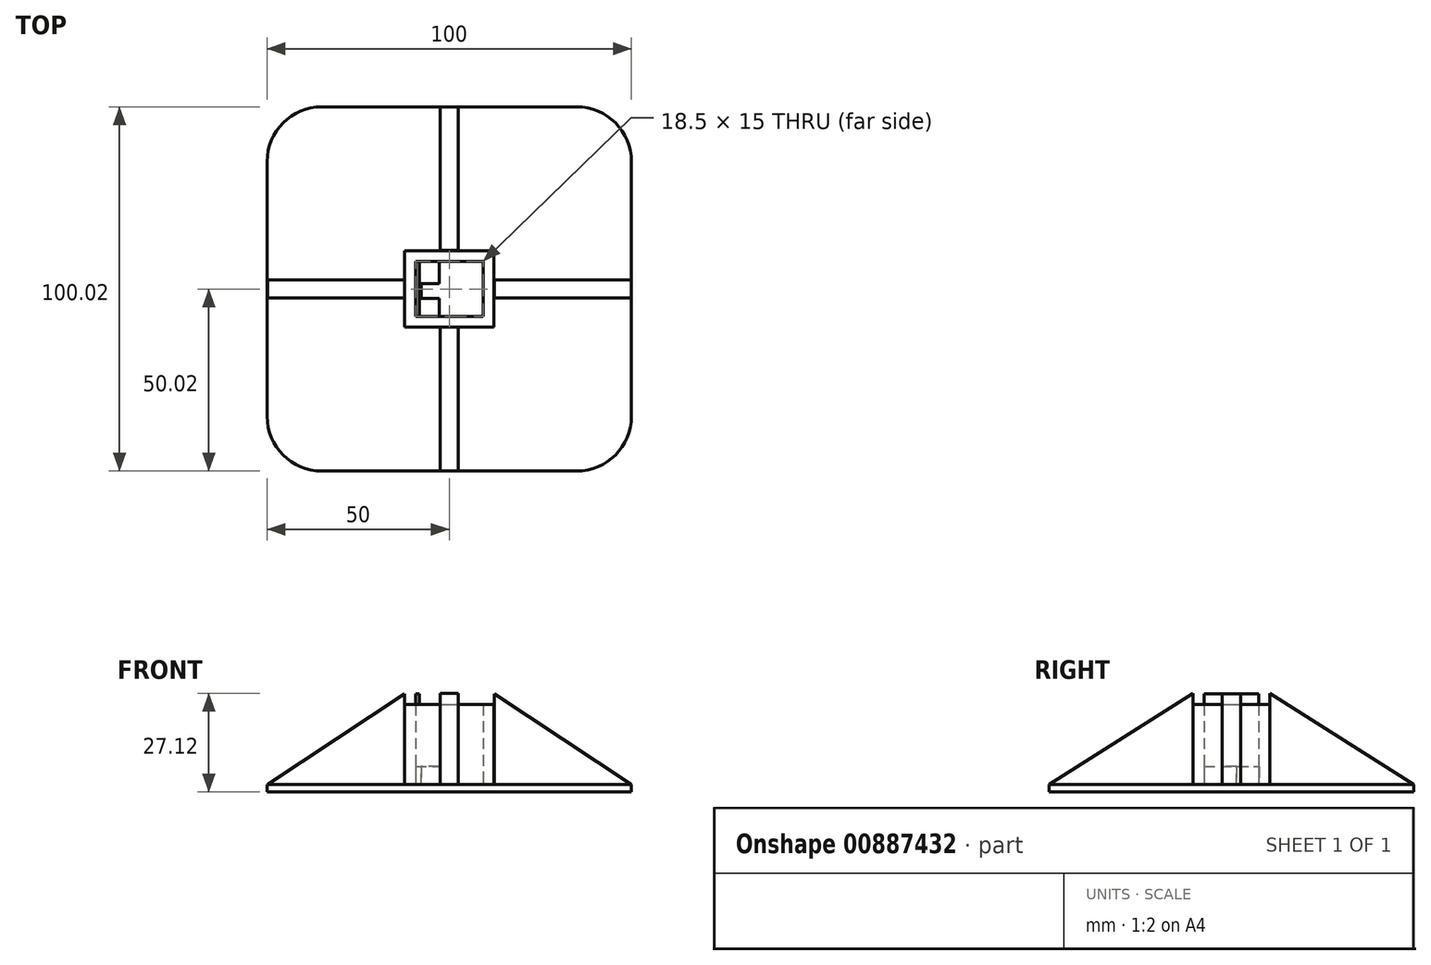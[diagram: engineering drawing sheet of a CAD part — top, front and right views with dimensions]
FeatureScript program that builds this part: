
annotation { "Feature Type Name" : "Feature", "Feature Type Description" : "" }
export const myFeature = defineFeature(function(context is Context, id is Id, definition is map)
    precondition{}
    {
        {
            var Q0;
            Q0=qCreatedBy(makeId("Top.planeOp"),FACE);
            var sketch = newSketch(context, id + "F0", { "sketchPlane" : qUnion([Q0])});
            skLineSegment(sketch, "E0.bottom", {"start": v(-50, -50) * mm, "end": v(50, -50) * mm});
            skLineSegment(sketch, "E0.top", {"start": v(-50, 50) * mm, "end": v(50, 50) * mm});
            skLineSegment(sketch, "E0.left", {"start": v(-50, -50) * mm, "end": v(-50, 50) * mm});
            skLineSegment(sketch, "E0.right", {"start": v(50, -50) * mm, "end": v(50, 50) * mm});
            skPoint(sketch, "E0.middle", {"position": v(0, 0) * mm});
            skSolve(sketch);
        }
        {
            var Q0;
            Q0=qCreatedBy(makeId("Top.planeOp"),FACE);
            var sketch = newSketch(context, id + "F1", { "sketchPlane" : qUnion([Q0])});
            skLineSegment(sketch, "E1.bottom", {"start": v(-9.25, -7.5) * mm, "end": v(9.25, -7.5) * mm});
            skLineSegment(sketch, "E1.top", {"start": v(-9.25, 7.5) * mm, "end": v(9.25, 7.5) * mm});
            skLineSegment(sketch, "E1.left", {"start": v(-9.25, -7.5) * mm, "end": v(-9.25, 7.5) * mm});
            skLineSegment(sketch, "E1.right", {"start": v(9.25, -7.5) * mm, "end": v(9.25, 7.5) * mm});
            skPoint(sketch, "E1.middle", {"position": v(0, 0) * mm});
            skLineSegment(sketch, "E2.0", {"start": v(-12.25, 10.5) * mm, "end": v(12.25, 10.5) * mm});
            skLineSegment(sketch, "E2.1", {"start": v(-12.25, -10.5) * mm, "end": v(-12.25, 10.5) * mm});
            skLineSegment(sketch, "E2.2", {"start": v(-12.25, -10.5) * mm, "end": v(12.25, -10.5) * mm});
            skLineSegment(sketch, "E2.3", {"start": v(12.25, -10.5) * mm, "end": v(12.25, 10.5) * mm});
            skSolve(sketch);
        }
        {
            var Q0;
            Q0 = qSketchRegion(id + "F1", true);
            extrude(context, id + "F2", {"entities" : qUnion([Q0]), "depth" : 22 * mm, "offsetDistance" : 25 * mm});
        }
        {
            var Q0;
            Q0=makeQuery(id+"F2.opExtrude","CAP_FACE",FACE,{"disambiguationData":[OSD([sQuery(id+"F1.wireOp",EDGE,"E1.bottom"),sQuery(id+"F1.wireOp",EDGE,"E1.top"),sQuery(id+"F1.wireOp",EDGE,"E1.left"),sQuery(id+"F1.wireOp",EDGE,"E1.right"),sQuery(id+"F1.wireOp",EDGE,"E2.0"),sQuery(id+"F1.wireOp",EDGE,"E2.1"),sQuery(id+"F1.wireOp",EDGE,"E2.2"),sQuery(id+"F1.wireOp",EDGE,"E2.3")])],"isStart":false});
            var sketch = newSketch(context, id + "F3", { "sketchPlane" : qUnion([Q0])});
            skLineSegment(sketch, "E3.bottom", {"start": v(-9.25, -7.5) * mm, "end": v(9.25, -7.5) * mm});
            skLineSegment(sketch, "E3.top", {"start": v(-9.25, 7.5) * mm, "end": v(9.25, 7.5) * mm});
            skLineSegment(sketch, "E3.left", {"start": v(-9.25, -7.5) * mm, "end": v(-9.25, 7.5) * mm});
            skLineSegment(sketch, "E3.right", {"start": v(9.25, -7.5) * mm, "end": v(9.25, 7.5) * mm});
            skPoint(sketch, "E3.middle", {"position": v(0, 0) * mm});
            skLineSegment(sketch, "E4.0", {"start": v(-8.25, -7.5) * mm, "end": v(-8.25, 7.5) * mm});
            skLineSegment(sketch, "E5.0", {"start": v(-12.25, 10.5) * mm, "end": v(12.25, 10.5) * mm});
            skLineSegment(sketch, "E5.1", {"start": v(-12.25, -10.5) * mm, "end": v(-12.25, 10.5) * mm});
            skLineSegment(sketch, "E5.2", {"start": v(-12.25, -10.5) * mm, "end": v(12.25, -10.5) * mm});
            skLineSegment(sketch, "E5.3", {"start": v(12.25, -10.5) * mm, "end": v(12.25, 10.5) * mm});
            skSolve(sketch);
        }
        {
            var Q0;
            {var subQ4=sQuery(id+"F3.wireOp",EDGE,"E3.left");Q0=makeQuery(id+"F3.imprint","IMPRINT",FACE,{"disambiguationData":[TD([[makeQuery(id+"F3.imprint","IMPRINT",EDGE,{"derivedFrom":subQ4}),1.0]])]});}
            var sketch = newSketch(context, id + "F4", { "sketchPlane" : qUnion([Q0])});
            skSolve(sketch);
        }
        {
            var Q0;
            {var subQ4=sQuery(id+"F3.wireOp",EDGE,"E3.left");Q0=makeQuery(id+"F4.imprint","IMPRINT",FACE,{"disambiguationData":[TD([[makeQuery(id+"F4.imprint","IMPRINT",EDGE,{"derivedFrom":makeQuery(id+"F3.imprint","IMPRINT",EDGE,{"derivedFrom":subQ4})}),1.0]])]});}
            var Q1;
            {var subQ0=sQuery(id+"F3.wireOp",EDGE,"E3.left");Q1=makeQuery(id+"F3.imprint","IMPRINT",FACE,{"disambiguationData":[TD([[makeQuery(id+"F3.imprint","IMPRINT",EDGE,{"derivedFrom":subQ0}),-1.0]])]});}
            extrude(context, id + "F5", {"entities" : qUnion([Q0, Q1]), "operationType" : NewBodyOperationType.ADD, "depth" : 3 * mm, "offsetDistance" : 25 * mm});
        }
        {
            var Q0;
            Q0=qCreatedBy(makeId("Top.planeOp"),FACE);
            var sketch = newSketch(context, id + "F6", { "sketchPlane" : qUnion([Q0])});
            skLineSegment(sketch, "E6", {"start": v(-2.74, 1.46) * mm, "end": v(-7.74, 1.46) * mm});
            skLineSegment(sketch, "E7", {"start": v(-7.74, -2.54) * mm, "end": v(-2.74, -2.54) * mm});
            skLineSegment(sketch, "E8", {"start": v(-7.74, 1.46) * mm, "end": v(-7.74, -2.54) * mm});
            skLineSegment(sketch, "E9", {"start": v(-2.74, 1.46) * mm, "end": v(-2.74, 7.55) * mm});
            skLineSegment(sketch, "E10", {"start": v(-2.74, -7.55) * mm, "end": v(-2.74, -2.54) * mm});
            skPoint(sketch, "E11.middle", {"position": v(0, 0) * mm});
            skLineSegment(sketch, "E12", {"start": v(-2.74, -7.55) * mm, "end": v(-9.27, -7.55) * mm});
            skLineSegment(sketch, "E13", {"start": v(-9.27, -7.55) * mm, "end": v(-9.27, 7.58) * mm});
            skLineSegment(sketch, "E14", {"start": v(-9.27, 7.58) * mm, "end": v(-2.74, 7.55) * mm});
            skSolve(sketch);
        }
        {
            var Q0;
            Q0 = qSketchRegion(id + "F6", true);
            extrude(context, id + "F7", {"entities" : qUnion([Q0]), "depth" : 5 * mm, "offsetDistance" : 25 * mm});
        }
        {
            var Q0;
            Q0=makeQuery(id+"F0.imprint","IMPRINT",FACE,{"disambiguationData":[TD([[makeQuery(id+"F0.imprint","IMPRINT",EDGE,{"derivedFrom":sQuery(id+"F0.wireOp",EDGE,"E0.bottom")}),1.0]])]});
            extrude(context, id + "F8", {"entities" : qUnion([Q0]), "oppositeDirection" : true, "depth" : 2 * mm, "offsetDistance" : 25 * mm});
        }
        {
            var Q0;
            Q0=qCreatedBy(makeId("Front.planeOp"),FACE);
            var sketch = newSketch(context, id + "F9", { "sketchPlane" : qUnion([Q0])});
            skLineSegment(sketch, "E15", {"start": v(-12.25, 25) * mm, "end": v(-49.93, 0) * mm});
            skLineSegment(sketch, "E16", {"start": v(-49.93, 0) * mm, "end": v(-12.25, 0) * mm});
            skLineSegment(sketch, "E17", {"start": v(-12.25, 0) * mm, "end": v(-12.25, 25) * mm});
            skLineSegment(sketch, "E18", {"start": v(12.3, 25) * mm, "end": v(49.92, 0) * mm});
            skLineSegment(sketch, "E19", {"start": v(49.92, 0) * mm, "end": v(12.3, 0) * mm});
            skLineSegment(sketch, "E20", {"start": v(12.3, 0) * mm, "end": v(12.3, 25) * mm});
            skSolve(sketch);
        }
        {
            var Q0;
            Q0 = qSketchRegion(id + "F9", true);
            extrude(context, id + "F10", {"entities" : qUnion([Q0]), "endBound" : BoundingType.SYMMETRIC, "depth" : 5 * mm, "offsetDistance" : 25 * mm});
        }
        {
            var Q0;
            Q0=qCreatedBy(makeId("Right.planeOp"),FACE);
            var sketch = newSketch(context, id + "F11", { "sketchPlane" : qUnion([Q0])});
            skLineSegment(sketch, "E21", {"start": v(-10.52, 25.12) * mm, "end": v(-50.02, 0) * mm});
            skLineSegment(sketch, "E22", {"start": v(-50.02, 0) * mm, "end": v(-10.52, 0) * mm});
            skLineSegment(sketch, "E23", {"start": v(-10.52, 0) * mm, "end": v(-10.52, 25.12) * mm});
            skLineSegment(sketch, "E24", {"start": v(10.56, 25.12) * mm, "end": v(50, 0) * mm});
            skLineSegment(sketch, "E25", {"start": v(50, 0) * mm, "end": v(10.56, 0) * mm});
            skLineSegment(sketch, "E26", {"start": v(10.56, 0) * mm, "end": v(10.56, 25.12) * mm});
            skSolve(sketch);
        }
        {
            var Q0;
            Q0 = qSketchRegion(id + "F11", true);
            extrude(context, id + "F12", {"entities" : qUnion([Q0]), "operationType" : NewBodyOperationType.ADD, "endBound" : BoundingType.SYMMETRIC, "depth" : 5 * mm, "offsetDistance" : 25 * mm});
        }
        {
            var Q0;
            Q0=makeQuery(id+"F8.opExtrude","SWEPT_EDGE",EDGE,{"disambiguationData":[OSD([sQuery(id+"F0.wireOp",EDGE,"E0.bottom"),sQuery(id+"F0.wireOp",EDGE,"E0.left")])]});
            var Q1;
            Q1=makeQuery(id+"F8.opExtrude","SWEPT_EDGE",EDGE,{"disambiguationData":[OSD([sQuery(id+"F0.wireOp",EDGE,"E0.bottom"),sQuery(id+"F0.wireOp",EDGE,"E0.right")])]});
            var Q2;
            Q2=makeQuery(id+"F8.opExtrude","SWEPT_EDGE",EDGE,{"disambiguationData":[OSD([sQuery(id+"F0.wireOp",EDGE,"E0.top"),sQuery(id+"F0.wireOp",EDGE,"E0.right")])]});
            var Q3;
            Q3=makeQuery(id+"F8.opExtrude","SWEPT_EDGE",EDGE,{"disambiguationData":[OSD([sQuery(id+"F0.wireOp",EDGE,"E0.top"),sQuery(id+"F0.wireOp",EDGE,"E0.left")])]});
            fillet(context, id + "F13", {"entities" : qUnion([Q0, Q1, Q2, Q3]), "radius" : 15 * mm, "tangentPropagation" : true, "allowEdgeOverflow" : false});
        }
    });
